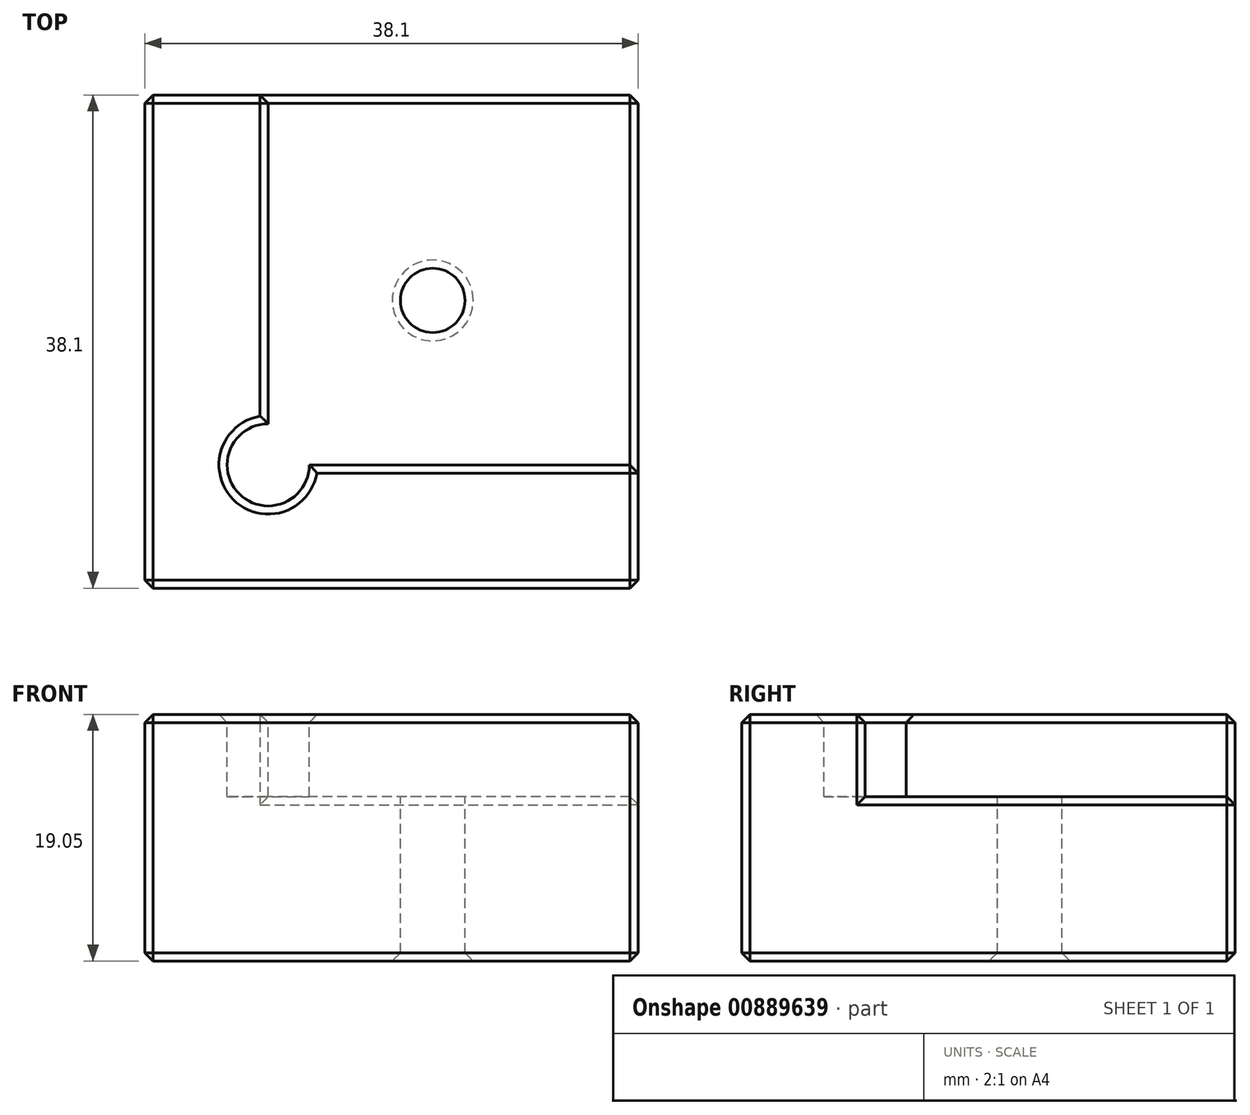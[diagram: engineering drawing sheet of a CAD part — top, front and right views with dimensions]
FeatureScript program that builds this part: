
annotation { "Feature Type Name" : "Feature", "Feature Type Description" : "" }
export const myFeature = defineFeature(function(context is Context, id is Id, definition is map)
    precondition{}
    {
        {
            var Q0;
            Q0=qCreatedBy(makeId("Top.planeOp"),FACE);
            var sketch = newSketch(context, id + "F0", { "sketchPlane" : qUnion([Q0])});
            skLineSegment(sketch, "E0.bottom", {"start": v(0, 0) * mm, "end": v(38.1, 0) * mm});
            skLineSegment(sketch, "E0.top", {"start": v(0, 38.1) * mm, "end": v(38.1, 38.1) * mm});
            skLineSegment(sketch, "E0.left", {"start": v(0, 0) * mm, "end": v(0, 38.1) * mm});
            skLineSegment(sketch, "E0.right", {"start": v(38.1, 0) * mm, "end": v(38.1, 38.1) * mm});
            skSolve(sketch);
        }
        {
            var Q0;
            Q0 = qSketchRegion(id + "F0", true);
            extrude(context, id + "F1", {"entities" : qUnion([Q0]), "depth" : 19.05 * mm, "offsetDistance" : 25.4 * mm});
        }
        {
            var Q0;
            Q0=makeQuery(id+"F1.opExtrude","CAP_FACE",FACE,{"disambiguationData":[OSD([sQuery(id+"F0.wireOp",EDGE,"E0.bottom"),sQuery(id+"F0.wireOp",EDGE,"E0.top"),sQuery(id+"F0.wireOp",EDGE,"E0.left"),sQuery(id+"F0.wireOp",EDGE,"E0.right")])],"isStart":false});
            var sketch = newSketch(context, id + "F2", { "sketchPlane" : qUnion([Q0])});
            skLineSegment(sketch, "E1.bottom", {"start": v(38.1, 38.1) * mm, "end": v(9.52, 38.1) * mm});
            skLineSegment(sketch, "E1.top", {"start": v(38.1, 9.53) * mm, "end": v(9.52, 9.53) * mm});
            skLineSegment(sketch, "E1.left", {"start": v(38.1, 38.1) * mm, "end": v(38.1, 9.53) * mm});
            skLineSegment(sketch, "E1.right", {"start": v(9.52, 38.1) * mm, "end": v(9.53, 9.53) * mm});
            skSolve(sketch);
        }
        {
            var Q0;
            Q0 = qSketchRegion(id + "F2", true);
            extrude(context, id + "F3", {"entities" : qUnion([Q0]), "operationType" : NewBodyOperationType.REMOVE, "oppositeDirection" : true, "depth" : 6.35 * mm, "offsetDistance" : 25.4 * mm});
        }
        {
            var Q0;
            Q0=makeQuery(id+"F3.boolean.opBoolean","COPY",FACE,{"derivedFrom":makeQuery(id+"F3.opExtrude","CAP_FACE",FACE,{"disambiguationData":[OSD([sQuery(id+"F2.wireOp",EDGE,"E1.bottom"),sQuery(id+"F2.wireOp",EDGE,"E1.top"),sQuery(id+"F2.wireOp",EDGE,"E1.left"),sQuery(id+"F2.wireOp",EDGE,"E1.right")])],"isStart":false})});
            var sketch = newSketch(context, id + "F4", { "sketchPlane" : qUnion([Q0])});
            skPoint(sketch, "E2", {"position": v(22.22, 22.23) * mm});
            skCircle(sketch, "E3", {"center": v(22.22, 22.23) * mm, "radius": 2.49 * mm});
            skSolve(sketch);
        }
        {
            var Q0;
            Q0 = qSketchRegion(id + "F4", true);
            extrude(context, id + "F5", {"entities" : qUnion([Q0]), "operationType" : NewBodyOperationType.REMOVE, "oppositeDirection" : true, "depth" : 25.4 * mm, "offsetDistance" : 25.4 * mm});
        }
        {
            var Q0;
            Q0=makeQuery(id+"F1.opExtrude","CAP_FACE",FACE,{"disambiguationData":[OSD([sQuery(id+"F0.wireOp",EDGE,"E0.bottom"),sQuery(id+"F0.wireOp",EDGE,"E0.top"),sQuery(id+"F0.wireOp",EDGE,"E0.left"),sQuery(id+"F0.wireOp",EDGE,"E0.right")])],"isStart":false});
            var sketch = newSketch(context, id + "F6", { "sketchPlane" : qUnion([Q0])});
            skCircle(sketch, "E4", {"center": v(9.52, 9.53) * mm, "radius": 3.18 * mm});
            skSolve(sketch);
        }
        {
            var Q0;
            Q0 = qSketchRegion(id + "F6", true);
            extrude(context, id + "F7", {"entities" : qUnion([Q0]), "operationType" : NewBodyOperationType.REMOVE, "oppositeDirection" : true, "depth" : 6.35 * mm, "offsetDistance" : 25.4 * mm});
        }
        {
            var Q0;
            Q0=makeQuery(id+"F3.boolean.opBoolean","COPY",EDGE,{"derivedFrom":makeQuery(id+"F3.opExtrude","CAP_EDGE",EDGE,{"disambiguationData":[OSD([sQuery(id+"F2.wireOp",EDGE,"E1.right")])],"isStart":true})});
            var Q1;
            Q1=makeQuery(id+"F7.boolean.opBoolean","COPY",EDGE,{"derivedFrom":makeQuery(id+"F7.opExtrude","CAP_EDGE",EDGE,{"disambiguationData":[OSD([sQuery(id+"F6.wireOp",EDGE,"E4")])],"isStart":true})});
            var Q2;
            Q2=makeQuery(id+"F3.boolean.opBoolean","COPY",EDGE,{"derivedFrom":makeQuery(id+"F3.opExtrude","CAP_EDGE",EDGE,{"disambiguationData":[OSD([sQuery(id+"F2.wireOp",EDGE,"E1.top")])],"isStart":true})});
            var Q3;
            Q3=makeQuery(id+"F1.opExtrude","CAP_FACE",FACE,{"disambiguationData":[OSD([sQuery(id+"F0.wireOp",EDGE,"E0.bottom"),sQuery(id+"F0.wireOp",EDGE,"E0.top"),sQuery(id+"F0.wireOp",EDGE,"E0.left"),sQuery(id+"F0.wireOp",EDGE,"E0.right")])],"isStart":false});
            var Q4;
            Q4=makeQuery(id+"F1.opExtrude","SWEPT_FACE",FACE,{"disambiguationData":[OSD([sQuery(id+"F0.wireOp",EDGE,"E0.left")])]});
            var Q5;
            Q5=makeQuery(id+"F1.opExtrude","SWEPT_FACE",FACE,{"disambiguationData":[OSD([sQuery(id+"F0.wireOp",EDGE,"E0.bottom")])]});
            var Q6;
            Q6=makeQuery(id+"F1.opExtrude","CAP_FACE",FACE,{"disambiguationData":[OSD([sQuery(id+"F0.wireOp",EDGE,"E0.bottom"),sQuery(id+"F0.wireOp",EDGE,"E0.top"),sQuery(id+"F0.wireOp",EDGE,"E0.left"),sQuery(id+"F0.wireOp",EDGE,"E0.right")])],"isStart":true});
            var Q7;
            Q7=makeQuery(id+"F1.opExtrude","SWEPT_FACE",FACE,{"disambiguationData":[OSD([sQuery(id+"F0.wireOp",EDGE,"E0.right")])]});
            var Q8;
            Q8=makeQuery(id+"F1.opExtrude","SWEPT_FACE",FACE,{"disambiguationData":[OSD([sQuery(id+"F0.wireOp",EDGE,"E0.top")])]});
            var Q9;
            Q9=makeQuery(id+"F5.boolean.opBoolean","COPY",EDGE,{"derivedFrom":makeQuery(id+"F5.opExtrude","CAP_EDGE",EDGE,{"disambiguationData":[OSD([sQuery(id+"F4.wireOp",EDGE,"E3")])],"isStart":true})});
            chamfer(context, id + "F8", {"entities" : qUnion([Q0, Q1, Q2, Q3, Q4, Q5, Q6, Q7, Q8, Q9]), "width" : 0.64 * mm, "tangentPropagation" : true});
        }
    });
